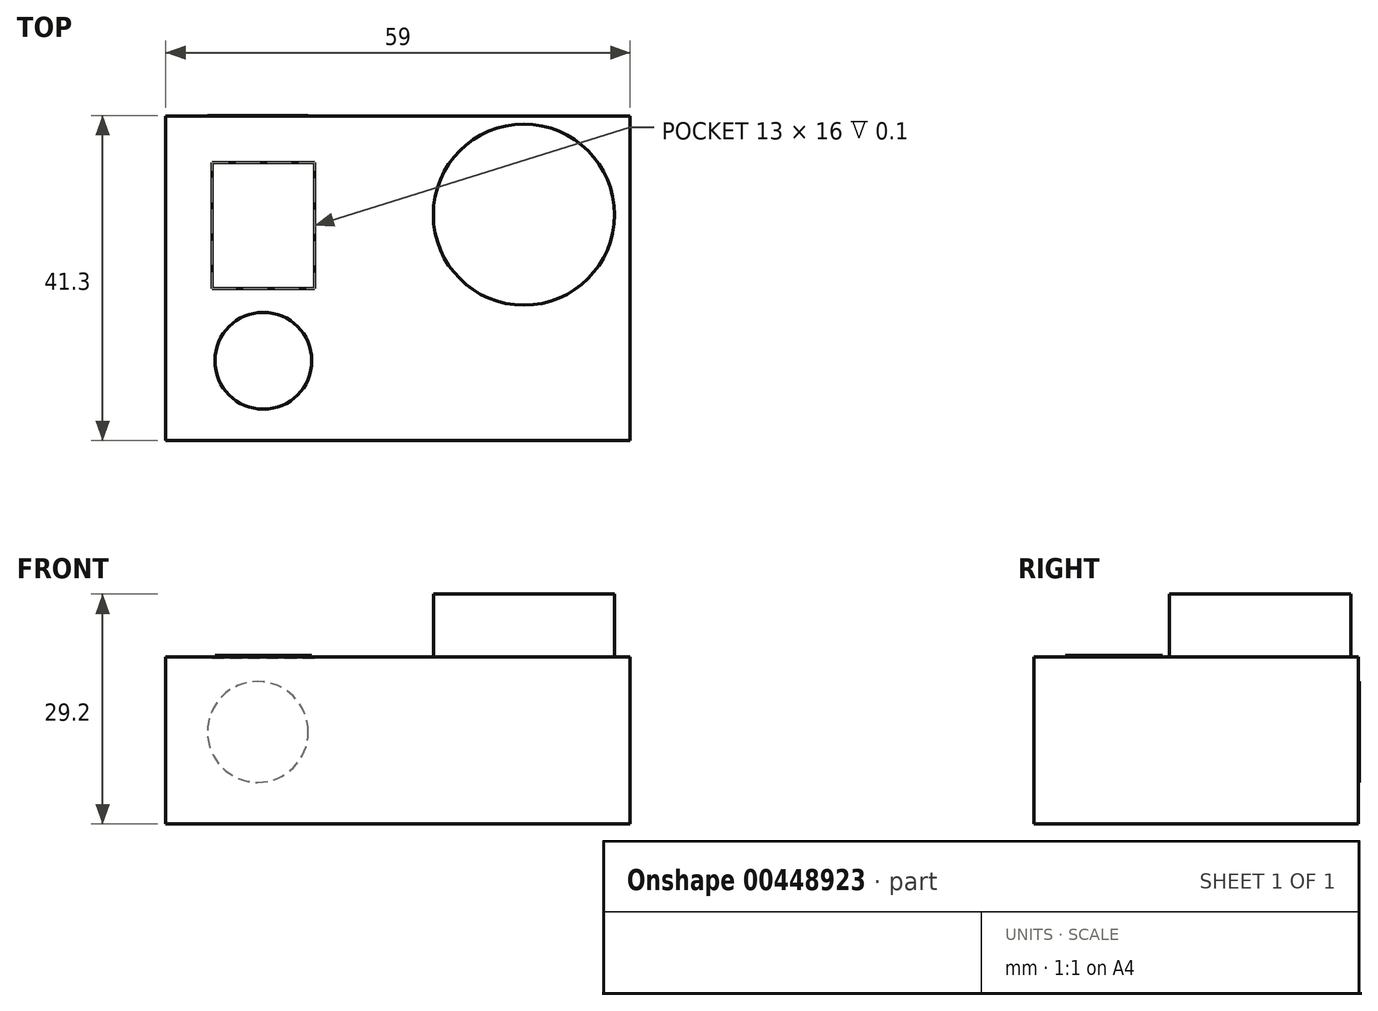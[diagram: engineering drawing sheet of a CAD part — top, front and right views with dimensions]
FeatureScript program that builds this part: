
annotation { "Feature Type Name" : "Feature", "Feature Type Description" : "" }
export const myFeature = defineFeature(function(context is Context, id is Id, definition is map)
    precondition{}
    {
        {
            var Q0;
            Q0=qCreatedBy(makeId("Top.planeOp"),FACE);
            var sketch = newSketch(context, id + "F0", { "sketchPlane" : qUnion([Q0])});
            skLineSegment(sketch, "E0.bottom", {"start": v(29.5, -20.6) * mm, "end": v(-29.5, -20.6) * mm});
            skLineSegment(sketch, "E0.top", {"start": v(29.5, 20.6) * mm, "end": v(-29.5, 20.6) * mm});
            skLineSegment(sketch, "E0.left", {"start": v(29.5, -20.6) * mm, "end": v(29.5, 20.6) * mm});
            skLineSegment(sketch, "E0.right", {"start": v(-29.5, -20.6) * mm, "end": v(-29.5, 20.6) * mm});
            skPoint(sketch, "E0.middle", {"position": v(0, 0) * mm});
            skSolve(sketch);
        }
        {
            var Q0;
            Q0 = qSketchRegion(id + "F0", true);
            extrude(context, id + "F1", {"entities" : qUnion([Q0]), "depth" : 21.2 * mm});
        }
        {
            var Q0;
            Q0=makeQuery(id+"F1.opExtrude","CAP_FACE",FACE,{"disambiguationData":[OSD([sQuery(id+"F0.wireOp",EDGE,"E0.bottom"),sQuery(id+"F0.wireOp",EDGE,"E0.top"),sQuery(id+"F0.wireOp",EDGE,"E0.left"),sQuery(id+"F0.wireOp",EDGE,"E0.right")])],"isStart":false});
            var sketch = newSketch(context, id + "F2", { "sketchPlane" : qUnion([Q0])});
            skCircle(sketch, "E1", {"center": v(16, 8.1) * mm, "radius": 11.5 * mm});
            skLineSegment(sketch, "E2", {"start": v(16, 19.6) * mm, "end": v(16, 20.6) * mm, "construction": true});
            skPoint(sketch, "E2.endSnap0", {"position": v(0, 20.6) * mm});
            skLineSegment(sketch, "E3", {"start": v(27.5, 8.1) * mm, "end": v(29.5, 8.1) * mm, "construction": true});
            skSolve(sketch);
        }
        {
            var Q0;
            Q0 = qSketchRegion(id + "F2", true);
            extrude(context, id + "F3", {"entities" : qUnion([Q0]), "operationType" : NewBodyOperationType.ADD, "depth" : 8 * mm});
        }
        {
            var Q0;
            Q0=makeQuery(id+"F1.opExtrude","SWEPT_FACE",FACE,{"disambiguationData":[OSD([sQuery(id+"F0.wireOp",EDGE,"E0.top")])]});
            var sketch = newSketch(context, id + "F4", { "sketchPlane" : qUnion([Q0])});
            skCircle(sketch, "E4", {"center": v(17.8, 11.7) * mm, "radius": 6.4 * mm});
            skLineSegment(sketch, "E5", {"start": v(24.2, 11.7) * mm, "end": v(29.5, 11.7) * mm, "construction": true});
            skLineSegment(sketch, "E6", {"start": v(17.8, 18.1) * mm, "end": v(17.8, 21.2) * mm, "construction": true});
            skSolve(sketch);
        }
        {
            var Q0;
            Q0 = qSketchRegion(id + "F4", true);
            extrude(context, id + "F5", {"entities" : qUnion([Q0]), "operationType" : NewBodyOperationType.ADD, "depth" : .1 * mm});
        }
        {
            var Q0;
            Q0=makeQuery(id+"F1.opExtrude","CAP_FACE",FACE,{"disambiguationData":[OSD([sQuery(id+"F0.wireOp",EDGE,"E0.bottom"),sQuery(id+"F0.wireOp",EDGE,"E0.top"),sQuery(id+"F0.wireOp",EDGE,"E0.left"),sQuery(id+"F0.wireOp",EDGE,"E0.right")])],"isStart":false});
            var sketch = newSketch(context, id + "F6", { "sketchPlane" : qUnion([Q0])});
            skLineSegment(sketch, "E7.bottom", {"start": v(-23.6, 14.7) * mm, "end": v(-10.6, 14.7) * mm});
            skLineSegment(sketch, "E7.top", {"start": v(-23.6, -1.3) * mm, "end": v(-10.6, -1.3) * mm});
            skLineSegment(sketch, "E7.left", {"start": v(-23.6, 14.7) * mm, "end": v(-23.6, -1.3) * mm});
            skLineSegment(sketch, "E7.right", {"start": v(-10.6, 14.7) * mm, "end": v(-10.6, -1.3) * mm});
            skLineSegment(sketch, "E8", {"start": v(-23.6, 14.7) * mm, "end": v(-29.5, 14.7) * mm, "construction": true});
            skLineSegment(sketch, "E9", {"start": v(-23.6, 14.7) * mm, "end": v(-23.6, 20.6) * mm, "construction": true});
            skSolve(sketch);
        }
        {
            var Q0;
            Q0=makeQuery(id+"F6.imprint","IMPRINT",FACE,{"disambiguationData":[TD([[makeQuery(id+"F6.imprint","IMPRINT",EDGE,{"derivedFrom":sQuery(id+"F6.wireOp",EDGE,"E7.bottom")}),-1.0]])]});
            extrude(context, id + "F7", {"entities" : qUnion([Q0]), "operationType" : NewBodyOperationType.REMOVE, "oppositeDirection" : true, "depth" : .1 * mm});
        }
        {
            var Q0;
            Q0=makeQuery(id+"F1.opExtrude","CAP_FACE",FACE,{"disambiguationData":[OSD([sQuery(id+"F0.wireOp",EDGE,"E0.bottom"),sQuery(id+"F0.wireOp",EDGE,"E0.top"),sQuery(id+"F0.wireOp",EDGE,"E0.left"),sQuery(id+"F0.wireOp",EDGE,"E0.right")])],"isStart":false});
            var sketch = newSketch(context, id + "F8", { "sketchPlane" : qUnion([Q0])});
            skCircle(sketch, "E10", {"center": v(-17.1, -10.45) * mm, "radius": 6.15 * mm});
            skPoint(sketch, "E10.centerSnap0", {"position": v(-17.1, -1.3) * mm});
            skLineSegment(sketch, "E11", {"start": v(-17.1, -16.6) * mm, "end": v(-17.1, -20.6) * mm, "construction": true});
            skSolve(sketch);
        }
        {
            var Q0;
            Q0 = qSketchRegion(id + "F8", true);
            extrude(context, id + "F9", {"entities" : qUnion([Q0]), "operationType" : NewBodyOperationType.ADD, "depth" : .2 * mm});
        }
    });
